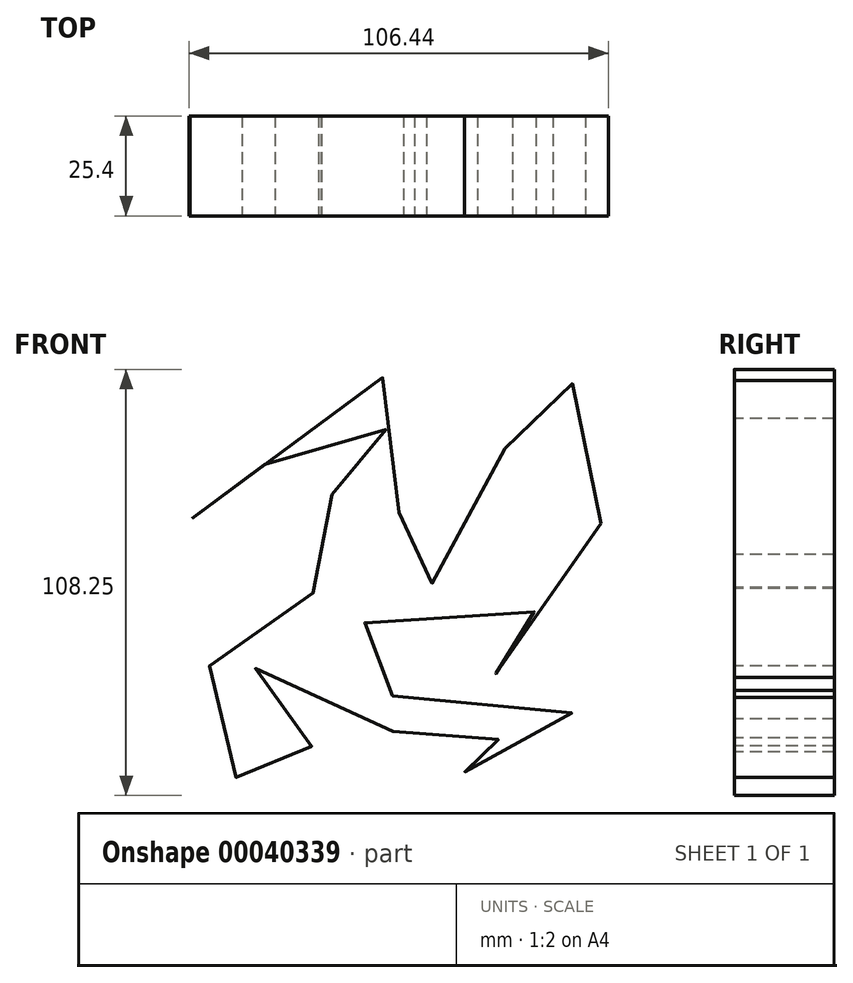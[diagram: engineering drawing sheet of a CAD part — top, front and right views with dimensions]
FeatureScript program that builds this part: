
annotation { "Feature Type Name" : "Feature", "Feature Type Description" : "" }
export const myFeature = defineFeature(function(context is Context, id is Id, definition is map)
    precondition{}
    {
        {
            var Q0;
            Q0=qCreatedBy(makeId("Front.planeOp"),FACE);
            var sketch = newSketch(context, id + "F0", { "sketchPlane" : qUnion([Q0])});
            skFitSpline(sketch, "E0", {"points": [v(-59.7, 6.3) * mm, v(-19.9, 44.14) * mm, v(11.5, 12.47) * mm, v(-27.46, 5.75) * mm, v(14.57, -10.79) * mm, v(25.22, 16.67) * mm, v(9.8, 37.13) * mm, v(40.92, 39.37) * mm, v(45.96, 27.32) * mm, v(42.88, -4.06) * mm, v(27.46, -30.13) * mm, v(0, -31.53) * mm, v(31.83, -13.93) * mm, v(-12.85, -18.68) * mm, v(-26.26, -36) * mm, v(-8.94, -38.79) * mm, v(16.2, -37.67) * mm, v(40.21, -47.45) * mm, v(16.75, -59.46) * mm, v(2.5, -54.7) * mm, v(-3.08, -53.03) * mm, v(21.5, -48.57) * mm, v(2.23, -44.65) * mm, v(-10.62, -48.57) * mm, v(-25.98, -46.05) * mm, v(-46.37, -31.53) * mm, v(-38.36, -52.3) * mm, v(-27.98, -51.7) * mm, v(-29.17, -60.9) * mm, v(-44.3, -62.08) * mm, v(-60.31, -43.99) * mm, v(-57.64, -35.98) * mm, v(-49.04, -24.7) * mm, v(-26.8, -15.5) * mm, v(-37.17, -5.13) * mm, v(-33.02, 10.3) * mm, v(-12.85, 13.56) * mm, v(-6.03, 21.86) * mm, v(-11.66, 29.58) * mm, v(-28.87, 30.76) * mm, v(-42.22, 18.6) * mm, v(-57.64, -2.76) * mm, v(-59.7, 6.3) * mm]});
            skSolve(sketch);
        }
        {
            var Q0;
            Q0=sQuery(id+"F0.wireOp",EDGE,"E0");
            extrude(context, id + "F1", {"bodyType" : ToolBodyType.SURFACE, "surfaceEntities" : qUnion([Q0]), "depth" : 25.4 * mm});
        }
    });
